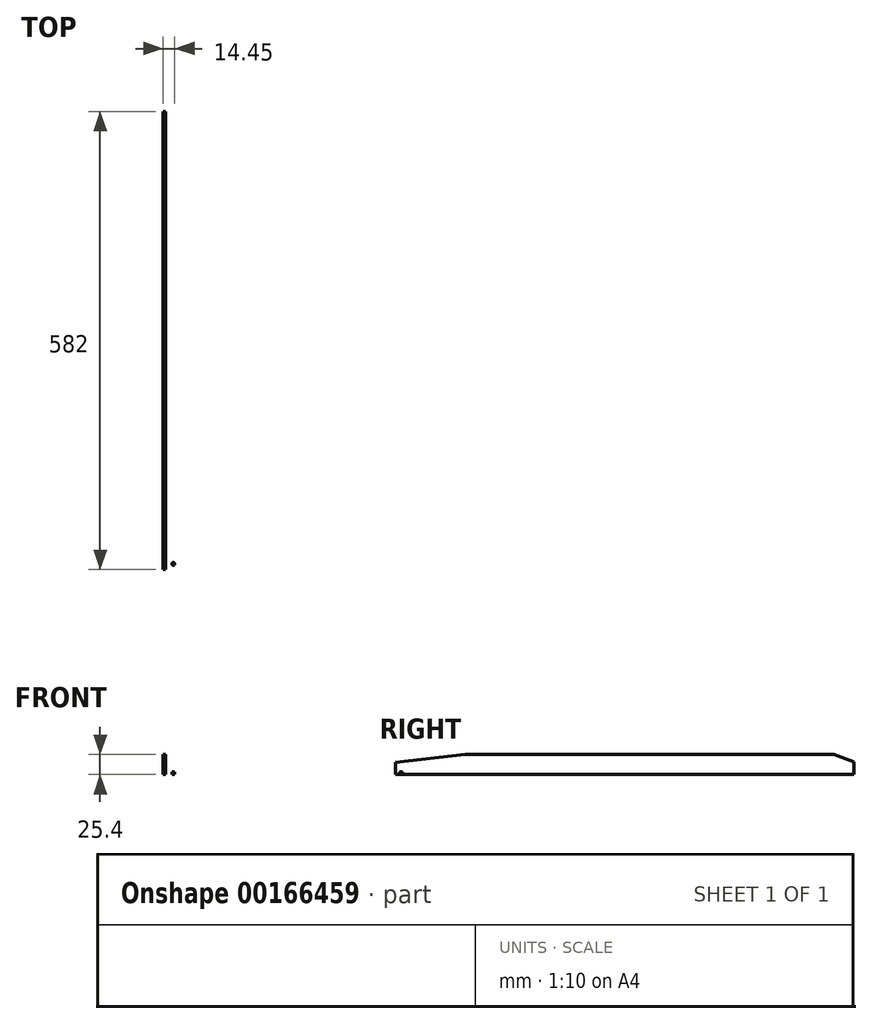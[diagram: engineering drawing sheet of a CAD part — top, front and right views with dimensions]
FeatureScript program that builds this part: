
annotation { "Feature Type Name" : "Feature", "Feature Type Description" : "" }
export const myFeature = defineFeature(function(context is Context, id is Id, definition is map)
    precondition{}
    {
        {
            var Q0;
            Q0=qCreatedBy(makeId("Front.planeOp"),FACE);
            var sketch = newSketch(context, id + "F0", { "sketchPlane" : qUnion([Q0])});
            skLineSegment(sketch, "E0.bottom", {"start": v(-12.7, 12.7) * mm, "end": v(-9.5, 12.7) * mm});
            skLineSegment(sketch, "E0.top", {"start": v(-12.7, -12.7) * mm, "end": v(12.7, -12.7) * mm});
            skLineSegment(sketch, "E0.left", {"start": v(-12.7, 12.7) * mm, "end": v(-12.7, -12.7) * mm});
            skLineSegment(sketch, "E0.right", {"start": v(12.7, -9.5) * mm, "end": v(12.7, -12.7) * mm});
            skPoint(sketch, "E0.middle", {"position": v(0, 0) * mm});
            skLineSegment(sketch, "E1", {"start": v(-9.5, 12.7) * mm, "end": v(-9.5, -9.5) * mm});
            skLineSegment(sketch, "E2", {"start": v(-9.5, -9.5) * mm, "end": v(12.7, -9.5) * mm});
            skPoint(sketch, "E3.orphan", {"position": v(12.7, 12.7) * mm});
            skSolve(sketch);
        }
        {
            var Q0;
            Q0 = qSketchRegion(id + "F0", true);
            extrude(context, id + "F1", {"entities" : qUnion([Q0]), "endBound" : BoundingType.SYMMETRIC, "depth" : 582 * mm});
        }
        {
            var Q0;
            Q0=makeQuery(id+"F1.opExtrude","CAP_EDGE",EDGE,{"disambiguationData":[OSD([sQuery(id+"F0.wireOp",EDGE,"E0.bottom")])],"isStart":false});
            chamfer(context, id + "F2", {"entities" : qUnion([Q0]), "chamferType" : ChamferType.TWO_OFFSETS, "width1" : 88 * mm, "oppositeDirection" : false, "width2" : 10.1 * mm, "tangentPropagation" : true});
        }
        {
            var Q0;
            Q0=makeQuery(id+"F1.opExtrude","CAP_EDGE",EDGE,{"disambiguationData":[OSD([sQuery(id+"F0.wireOp",EDGE,"E0.bottom")])],"isStart":true});
            chamfer(context, id + "F3", {"entities" : qUnion([Q0]), "chamferType" : ChamferType.TWO_OFFSETS, "width1" : 9.5 * mm, "oppositeDirection" : false, "width2" : 25 * mm, "tangentPropagation" : true});
        }
        {
            var Q0;
            Q0=makeQuery(id+"F1.opExtrude","SWEPT_FACE",FACE,{"disambiguationData":[OSD([sQuery(id+"F0.wireOp",EDGE,"E2")])]});
            var sketch = newSketch(context, id + "F4", { "sketchPlane" : qUnion([Q0])});
            skCircle(sketch, "E4", {"center": v(0, 283.8) * mm, "radius": 1.75 * mm});
            skCircle(sketch, "E5.MirrorC", {"center": v(0, -283.8) * mm, "radius": 1.75 * mm});
            skSolve(sketch);
        }
        {
            var Q0;
            Q0=makeQuery(id+"F4.imprint","IMPRINT",FACE,{"disambiguationData":[TD([[makeQuery(id+"F4.imprint","IMPRINT",EDGE,{"derivedFrom":sQuery(id+"F4.wireOp",EDGE,"E5.MirrorC")}),-1.0]])]});
            var Q1;
            Q1=makeQuery(id+"F4.imprint","IMPRINT",FACE,{"disambiguationData":[TD([[makeQuery(id+"F4.imprint","IMPRINT",EDGE,{"derivedFrom":sQuery(id+"F4.wireOp",EDGE,"E4")}),1.0]])]});
            extrude(context, id + "F5", {"entities" : qUnion([Q0, Q1]), "operationType" : NewBodyOperationType.REMOVE, "endBound" : BoundingType.UP_TO_NEXT, "oppositeDirection" : true, "depth" : 25 * mm});
        }
    });
